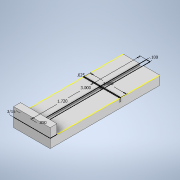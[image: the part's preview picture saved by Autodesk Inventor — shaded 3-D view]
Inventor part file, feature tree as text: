
AUTODESK INVENTOR PART (.ipt)
format: ipt  version: 2020 (Build 240168000, 168)  size: 135,168 bytes
history: native  units: in
note: dims shown in document units (in); Inventor stores cm internally (conversion verified against a paired STEP export)
features: extrude x4, sketch x2
ambient origin geometry x8: Origin, YZ Plane, XZ Plane, XY Plane, X Axis, Y Axis, Z Axis, Center Point
bodies: Solid1 (feature_tree)
feature tree (6):
  extrude  "Extrusion1"  Depth=3.0in
  sketch  "Sketch2"  dims[d2=0.25in d3=0.0in d4=0.1875in d5=0.05in d6=0.1in d7=3.0in d8=1.72in d9=1.0in d10=0.025in d11=0.25in d12=0.0in d13=0.05in d14=0.0in d15=0.1in d16=0.0in]
  extrude  "Extrusion2"  Depth=0.1875in
  extrude  "Extrusion3"  Depth=0.05in
  extrude  "Extrusion4"  Depth=0.1in
  sketch  "Sketch1"  dims[d0=1.0in d1=3.0in]
